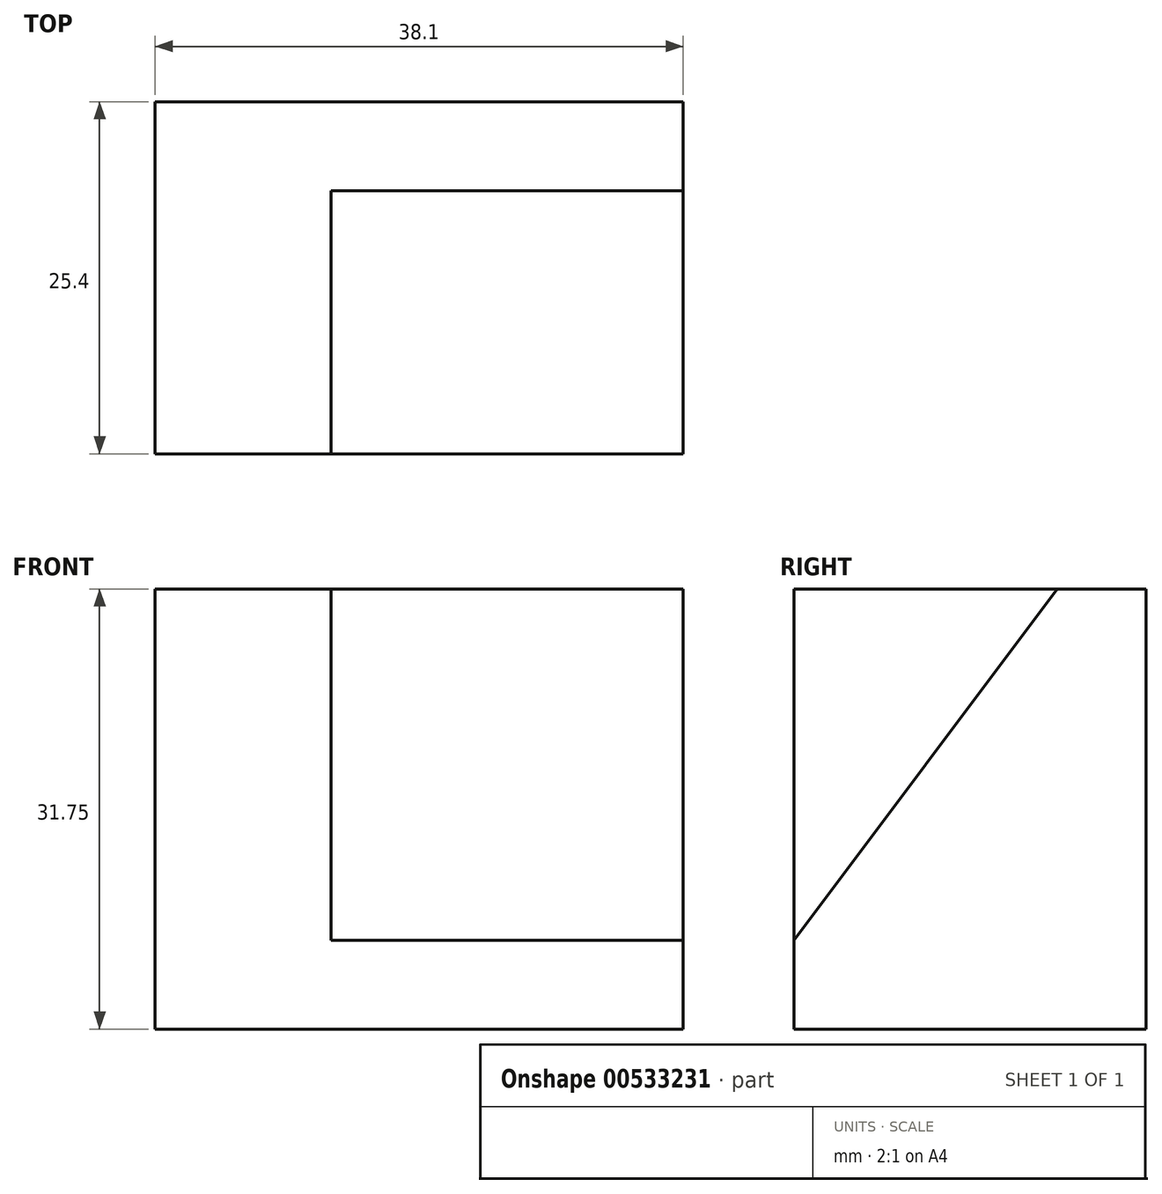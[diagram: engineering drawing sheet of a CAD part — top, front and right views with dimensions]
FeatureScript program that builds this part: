
annotation { "Feature Type Name" : "Feature", "Feature Type Description" : "" }
export const myFeature = defineFeature(function(context is Context, id is Id, definition is map)
    precondition{}
    {
        {
            var Q0;
            Q0=qCreatedBy(makeId("Front.planeOp"),FACE);
            var sketch = newSketch(context, id + "F0", { "sketchPlane" : qUnion([Q0])});
            skLineSegment(sketch, "E0.bottom", {"start": v(-62.87, 51.7) * mm, "end": v(-24.77, 51.7) * mm});
            skLineSegment(sketch, "E0.top", {"start": v(-62.87, 19.94) * mm, "end": v(-24.77, 19.94) * mm});
            skLineSegment(sketch, "E0.left", {"start": v(-62.87, 51.7) * mm, "end": v(-62.87, 19.94) * mm});
            skLineSegment(sketch, "E0.right", {"start": v(-24.77, 51.7) * mm, "end": v(-24.77, 19.94) * mm});
            skSolve(sketch);
        }
        {
            var Q0;
            Q0 = qSketchRegion(id + "F0", true);
            extrude(context, id + "F1", {"entities" : qUnion([Q0]), "depth" : 25.4 * mm, "offsetDistance" : 25.4 * mm});
        }
        {
            var Q0;
            Q0=makeQuery(id+"F1.opExtrude","SWEPT_FACE",FACE,{"disambiguationData":[OSD([sQuery(id+"F0.wireOp",EDGE,"E0.right")])]});
            var sketch = newSketch(context, id + "F2", { "sketchPlane" : qUnion([Q0])});
            skLineSegment(sketch, "E1", {"start": v(-6.43, 51.7) * mm, "end": v(-25.4, 26.33) * mm});
            skLineSegment(sketch, "E2", {"start": v(-25.4, 26.33) * mm, "end": v(-25.4, 51.7) * mm});
            skLineSegment(sketch, "E3", {"start": v(-25.4, 51.7) * mm, "end": v(-6.43, 51.7) * mm});
            skSolve(sketch);
        }
        {
            var Q0;
            Q0=makeQuery(id+"F2.imprint","IMPRINT",FACE,{"disambiguationData":[TD([[makeQuery(id+"F2.imprint","IMPRINT",EDGE,{"derivedFrom":sQuery(id+"F2.wireOp",EDGE,"E1")}),-1.0]])]});
            extrude(context, id + "F3", {"entities" : qUnion([Q0]), "operationType" : NewBodyOperationType.REMOVE, "oppositeDirection" : true, "depth" : 12.7 * mm, "offsetDistance" : 25.4 * mm});
        }
        {
            var Q0;
            Q0=makeQuery(id+"F3.boolean.opBoolean","COPY",FACE,{"derivedFrom":makeQuery(id+"F3.opExtrude","CAP_FACE",FACE,{"disambiguationData":[OSD([sQuery(id+"F2.wireOp",EDGE,"E1"),sQuery(id+"F2.wireOp",EDGE,"E2"),sQuery(id+"F2.wireOp",EDGE,"E3")])],"isStart":false})});
            extrude(context, id + "F4", {"entities" : qUnion([Q0]), "operationType" : NewBodyOperationType.REMOVE, "oppositeDirection" : true, "depth" : 12.7 * mm, "offsetDistance" : 25.4 * mm});
        }
    });
